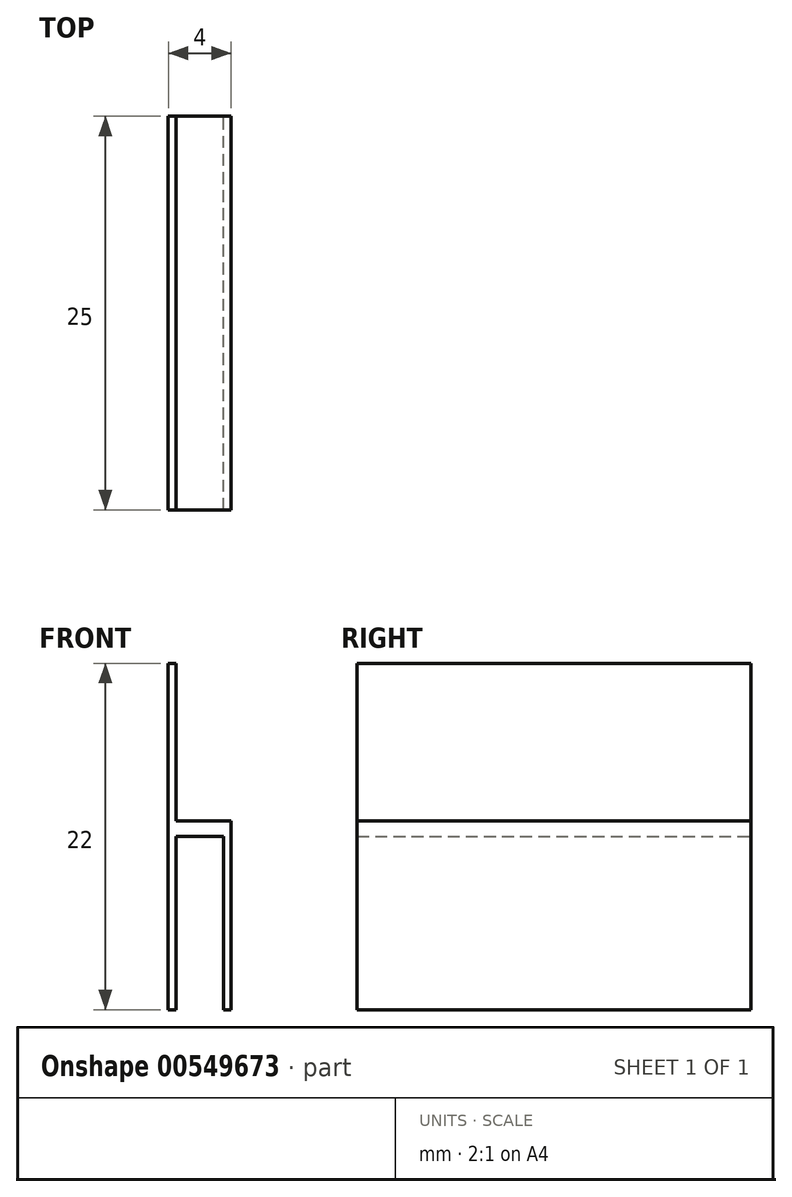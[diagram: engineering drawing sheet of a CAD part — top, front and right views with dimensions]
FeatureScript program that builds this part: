
annotation { "Feature Type Name" : "Feature", "Feature Type Description" : "" }
export const myFeature = defineFeature(function(context is Context, id is Id, definition is map)
    precondition{}
    {
        {
            var Q0;
            Q0=qCreatedBy(makeId("Front.planeOp"),FACE);
            var sketch = newSketch(context, id + "F0", { "sketchPlane" : qUnion([Q0])});
            skLineSegment(sketch, "E0.bottom", {"start": v(-33.7, 10.17) * mm, "end": v(-33.2, 10.17) * mm});
            skLineSegment(sketch, "E0.top", {"start": v(-33.7, -11.83) * mm, "end": v(-33.2, -11.83) * mm});
            skLineSegment(sketch, "E0.left", {"start": v(-33.7, 10.17) * mm, "end": v(-33.7, -11.83) * mm});
            skLineSegment(sketch, "E0.right", {"start": v(-33.2, 10.17) * mm, "end": v(-33.2, 0.17) * mm});
            skLineSegment(sketch, "E1.top", {"start": v(-30.2, -11.83) * mm, "end": v(-29.7, -11.83) * mm});
            skLineSegment(sketch, "E1.right", {"start": v(-29.7, 0.17) * mm, "end": v(-29.7, -11.83) * mm});
            skPoint(sketch, "E2.oppositeSnap0", {"position": v(-33.2, -0.83) * mm});
            skLineSegment(sketch, "E2.bottom", {"start": v(-33.2, 0.17) * mm, "end": v(-30.2, 0.17) * mm});
            skLineSegment(sketch, "E2.top", {"start": v(-33.2, -0.83) * mm, "end": v(-30.2, -0.83) * mm});
            skLineSegment(sketch, "E2.left", {"start": v(-33.2, 0.17) * mm, "end": v(-33.2, 0.17) * mm});
            skLineSegment(sketch, "E3", {"start": v(-33.2, -0.83) * mm, "end": v(-33.2, -11.83) * mm});
            skLineSegment(sketch, "E4", {"start": v(-30.2, -0.83) * mm, "end": v(-30.2, -11.83) * mm});
            skLineSegment(sketch, "E5", {"start": v(-30.2, 0.17) * mm, "end": v(-29.7, 0.17) * mm});
            skSolve(sketch);
        }
        {
            var Q0;
            Q0 = qSketchRegion(id + "F0", true);
            extrude(context, id + "F1", {"entities" : qUnion([Q0]), "depth" : 25 * mm, "offsetDistance" : 25 * mm});
        }
    });
